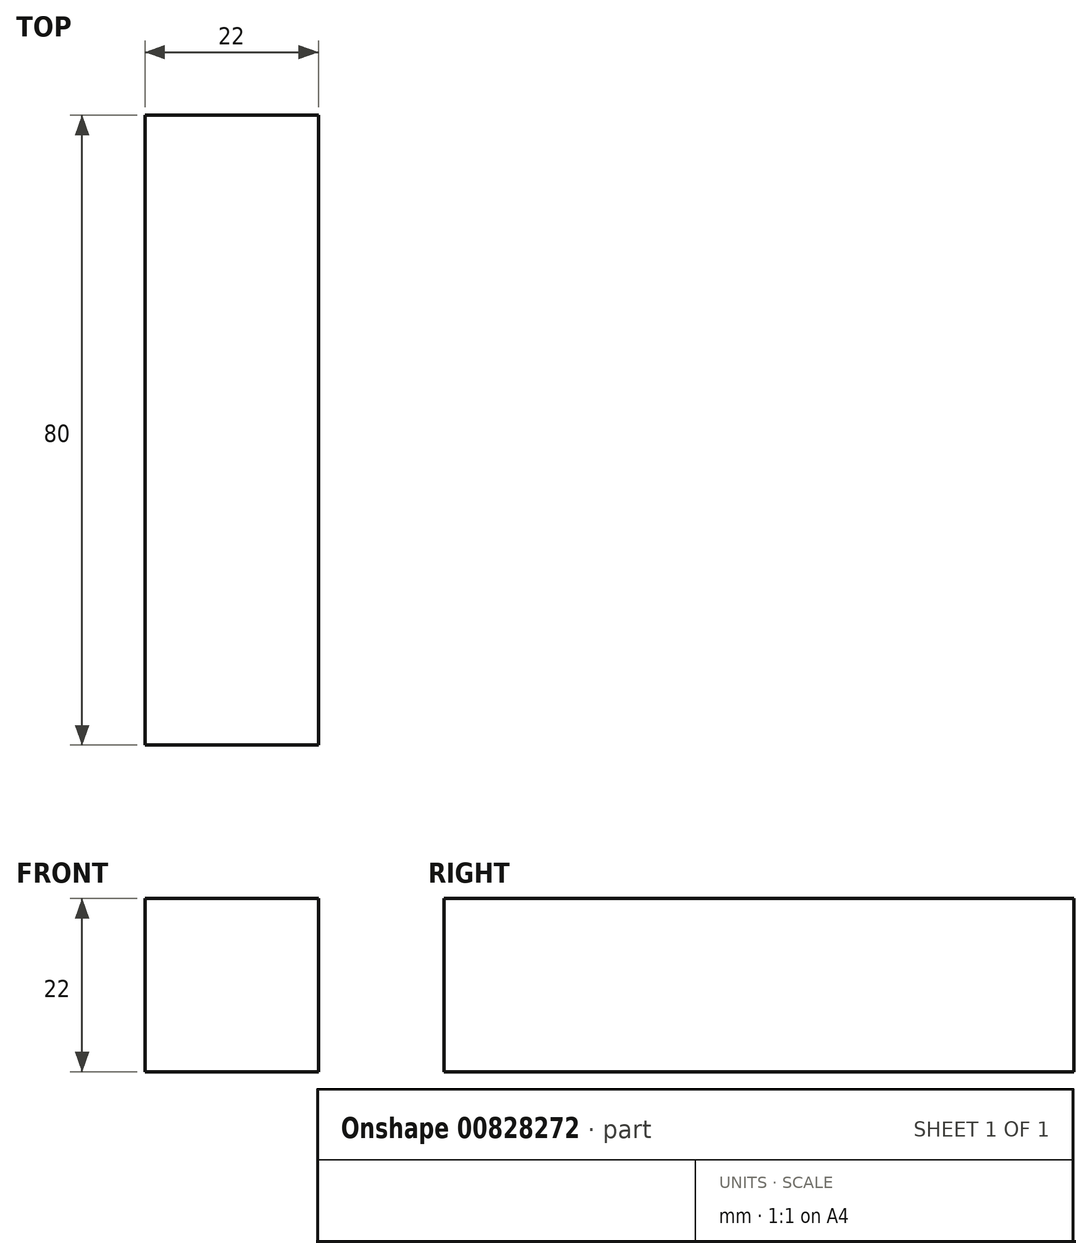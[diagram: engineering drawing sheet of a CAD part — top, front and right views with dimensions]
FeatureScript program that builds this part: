
annotation { "Feature Type Name" : "Feature", "Feature Type Description" : "" }
export const myFeature = defineFeature(function(context is Context, id is Id, definition is map)
    precondition{}
    {
        {
            var Q0;
            Q0=qCreatedBy(makeId("Front.planeOp"),FACE);
            var sketch = newSketch(context, id + "F0", { "sketchPlane" : qUnion([Q0])});
            skLineSegment(sketch, "E0.bottom", {"start": v(-11, -11) * mm, "end": v(11, -11) * mm});
            skLineSegment(sketch, "E0.top", {"start": v(-11, 11) * mm, "end": v(11, 11) * mm});
            skLineSegment(sketch, "E0.left", {"start": v(-11, -11) * mm, "end": v(-11, 11) * mm});
            skLineSegment(sketch, "E0.right", {"start": v(11, -11) * mm, "end": v(11, 11) * mm});
            skPoint(sketch, "E0.middle", {"position": v(0, 0) * mm});
            skSolve(sketch);
        }
        {
            var Q0;
            Q0=makeQuery(id+"F0.imprint","IMPRINT",FACE,{"disambiguationData":[TD([[makeQuery(id+"F0.imprint","IMPRINT",EDGE,{"derivedFrom":sQuery(id+"F0.wireOp",EDGE,"E0.bottom")}),1.0]])]});
            extrude(context, id + "F1", {"entities" : qUnion([Q0]), "endBound" : BoundingType.SYMMETRIC, "depth" : 80 * mm, "offsetDistance" : 25 * mm});
        }
    });
